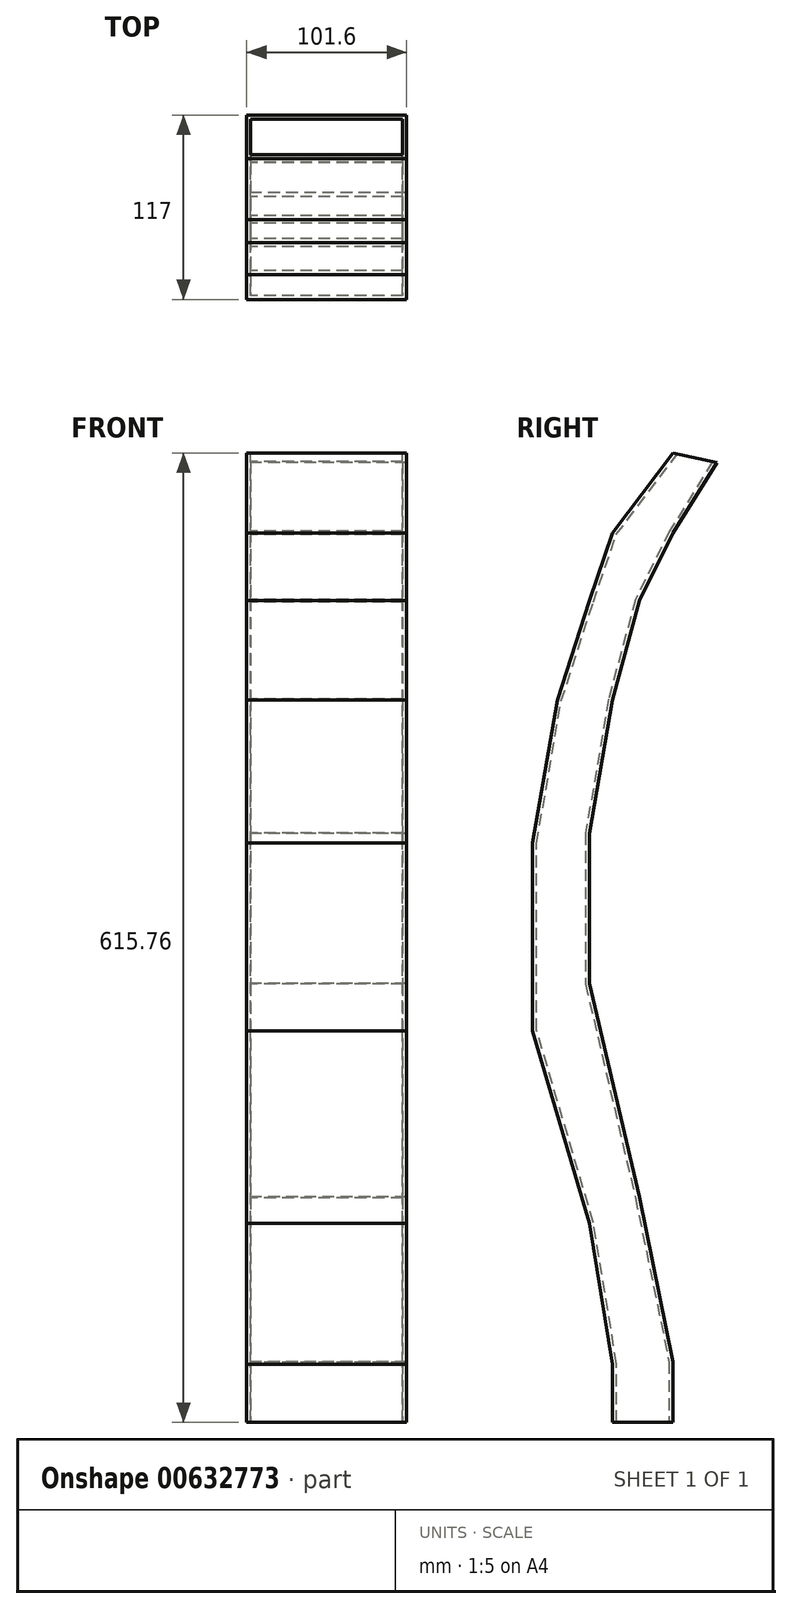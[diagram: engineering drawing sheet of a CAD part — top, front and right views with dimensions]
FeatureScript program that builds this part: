
annotation { "Feature Type Name" : "Feature", "Feature Type Description" : "" }
export const myFeature = defineFeature(function(context is Context, id is Id, definition is map)
    precondition{}
    {
        {
            var Q0;
            Q0=qCreatedBy(makeId("Right.planeOp"),FACE);
            var sketch = newSketch(context, id + "F0", { "sketchPlane" : qUnion([Q0])});
            skLineSegment(sketch, "E0", {"start": v(80.82, 360.99) * mm, "end": v(53.1, 316.35) * mm});
            skLineSegment(sketch, "E1", {"start": v(53.1, 316.35) * mm, "end": v(31.56, 273.24) * mm});
            skLineSegment(sketch, "E2", {"start": v(31.56, 273.24) * mm, "end": v(14.62, 210.13) * mm});
            skLineSegment(sketch, "E3", {"start": v(14.62, 210.13) * mm, "end": v(0, 125.46) * mm});
            skLineSegment(sketch, "E4", {"start": v(0, 125.46) * mm, "end": v(0, 30.02) * mm});
            skLineSegment(sketch, "E5", {"start": v(0, 30.02) * mm, "end": v(31.56, -105.45) * mm});
            skLineSegment(sketch, "E6", {"start": v(31.56, -105.45) * mm, "end": v(53.1, -210.13) * mm});
            skLineSegment(sketch, "E7", {"start": v(53.1, -210.13) * mm, "end": v(53.1, -248.61) * mm});
            skLineSegment(sketch, "E8", {"start": v(53.1, -248.61) * mm, "end": v(14.62, -248.61) * mm});
            skLineSegment(sketch, "E9", {"start": v(14.62, -248.61) * mm, "end": v(14.62, -211.67) * mm});
            skLineSegment(sketch, "E10", {"start": v(14.62, -211.67) * mm, "end": v(53.1, -210.13) * mm});
            skLineSegment(sketch, "E11", {"start": v(14.62, -211.67) * mm, "end": v(0, -122.38) * mm});
            skLineSegment(sketch, "E12", {"start": v(0, -122.38) * mm, "end": v(31.56, -105.45) * mm});
            skLineSegment(sketch, "E13", {"start": v(0, -122.38) * mm, "end": v(-36.18, 0) * mm});
            skLineSegment(sketch, "E14", {"start": v(-36.18, 0) * mm, "end": v(0, 30.02) * mm});
            skLineSegment(sketch, "E15", {"start": v(-36.18, 0) * mm, "end": v(-36.18, 119.3) * mm});
            skLineSegment(sketch, "E16", {"start": v(-36.18, 119.3) * mm, "end": v(0, 125.46) * mm});
            skLineSegment(sketch, "E17", {"start": v(-36.18, 119.3) * mm, "end": v(-20.49, 210.13) * mm});
            skLineSegment(sketch, "E18", {"start": v(-20.49, 210.13) * mm, "end": v(14.62, 210.13) * mm});
            skLineSegment(sketch, "E19", {"start": v(-20.49, 210.13) * mm, "end": v(0, 273.24) * mm});
            skLineSegment(sketch, "E20", {"start": v(0, 273.24) * mm, "end": v(31.56, 273.24) * mm});
            skLineSegment(sketch, "E21", {"start": v(0, 273.24) * mm, "end": v(14.62, 316.35) * mm});
            skLineSegment(sketch, "E22", {"start": v(14.62, 316.35) * mm, "end": v(53.1, 316.35) * mm});
            skLineSegment(sketch, "E23", {"start": v(14.62, 316.35) * mm, "end": v(53.1, 367.15) * mm});
            skLineSegment(sketch, "E24", {"start": v(80.82, 360.99) * mm, "end": v(53.1, 367.15) * mm});
            skSolve(sketch);
        }
        {
            var Q0;
            Q0 = qSketchRegion(id + "F0", true);
            extrude(context, id + "F1", {"entities" : qUnion([Q0]), "depth" : 101.6 * mm, "offsetDistance" : 25.4 * mm});
        }
        {
            var Q0;
            Q0=makeQuery(id+"F1.opExtrude","SWEPT_FACE",FACE,{"disambiguationData":[OSD([sQuery(id+"F0.wireOp",EDGE,"E24")])]});
            var Q1;
            Q1=makeQuery(id+"F1.opExtrude","SWEPT_FACE",FACE,{"disambiguationData":[OSD([sQuery(id+"F0.wireOp",EDGE,"E8")])]});
            shell(context, id + "F2", {"entities" : qUnion([Q0, Q1]), "thickness" : 2.54 * mm});
        }
    });
